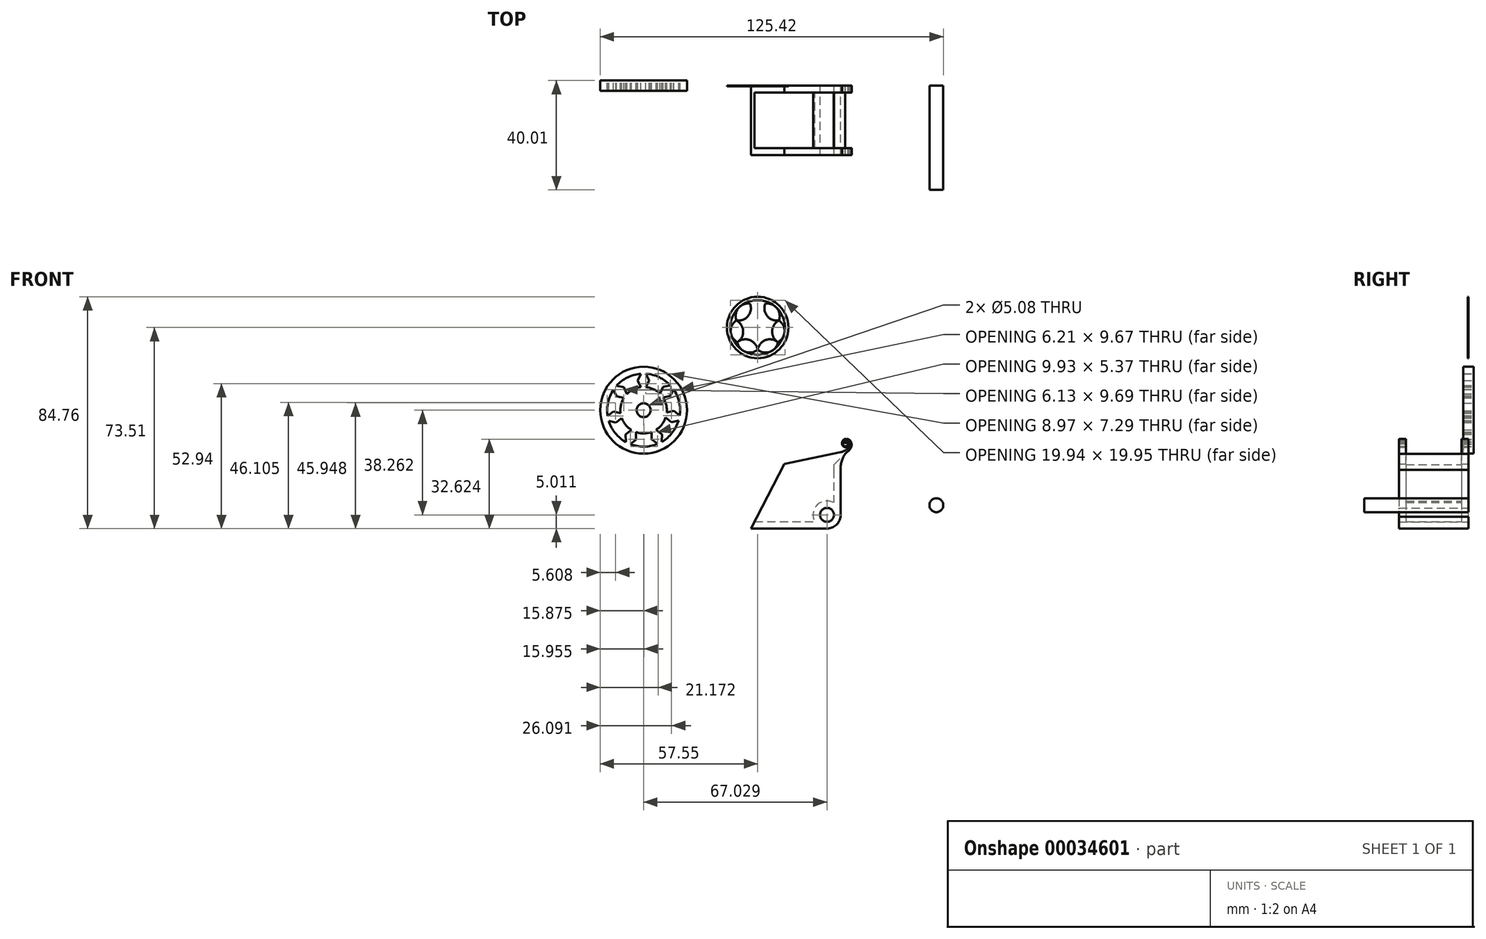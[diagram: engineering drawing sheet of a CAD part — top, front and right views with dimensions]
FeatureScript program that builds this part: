
annotation { "Feature Type Name" : "Feature", "Feature Type Description" : "" }
export const myFeature = defineFeature(function(context is Context, id is Id, definition is map)
    precondition{}
    {
        {
            var Q0;
            Q0=qCreatedBy(makeId("Front.planeOp"),FACE);
            var sketch = newSketch(context, id + "F0", { "sketchPlane" : qUnion([Q0])});
            skLineSegment(sketch, "E0", {"start": v(-14.54, -20.52) * mm, "end": v(13.23, -20.52) * mm});
            skLineSegment(sketch, "E1", {"start": v(18.2, 7.38) * mm, "end": v(-2.33, 3.11) * mm});
            skLineSegment(sketch, "E2", {"start": v(-2.33, 3.11) * mm, "end": v(-14.54, -20.52) * mm});
            skArc(sketch, "E3", {"start": v(13.23, -20.52) * mm, "mid": v(16.54, -19.27) * mm, "end": v(18.2, -16.16) * mm});
            skLineSegment(sketch, "E4.left", {"start": v(18.2, -0.57) * mm, "end": v(18.2, -0.57) * mm});
            skArc(sketch, "E5", {"start": v(18.2, 7.38) * mm, "mid": v(20.01, 8.1) * mm, "end": v(21.47, 9.4) * mm});
            skArc(sketch, "E6", {"start": v(21.47, 9.4) * mm, "mid": v(21.14, 11.42) * mm, "end": v(19.16, 10.9) * mm});
            skArc(sketch, "E7", {"start": v(19.16, 10.9) * mm, "mid": v(19.64, 9.63) * mm, "end": v(20.84, 10.26) * mm});
            skArc(sketch, "E8", {"start": v(20.84, 10.26) * mm, "mid": v(20.51, 10.8) * mm, "end": v(19.96, 10.48) * mm});
            skLineSegment(sketch, "E9", {"start": v(19.84, 6.78) * mm, "end": v(21.47, 8.34) * mm});
            skArc(sketch, "E10", {"start": v(21.47, 8.34) * mm, "mid": v(22.23, 10.05) * mm, "end": v(21.54, 11.8) * mm});
            skArc(sketch, "E11", {"start": v(21.54, 11.8) * mm, "mid": v(19.4, 11.99) * mm, "end": v(18.9, 9.88) * mm});
            skArc(sketch, "E12", {"start": v(18.9, 9.88) * mm, "mid": v(20.42, 9.3) * mm, "end": v(21.22, 10.7) * mm});
            skArc(sketch, "E13", {"start": v(21.22, 10.7) * mm, "mid": v(20.48, 11.2) * mm, "end": v(19.96, 10.48) * mm});
            skArc(sketch, "E14", {"start": v(19.84, 6.78) * mm, "mid": v(18.56, 4) * mm, "end": v(18.2, 0.95) * mm});
            skLineSegment(sketch, "E15.trimOffspring", {"start": v(18.2, 1.72) * mm, "end": v(18.2, -16.16) * mm});
            skPoint(sketch, "E16.end.orphan", {"position": v(18.2, 5.22) * mm});
            skCircle(sketch, "E17", {"center": v(13.23, -15.5) * mm, "radius": 2.54 * mm});
            skSolve(sketch);
        }
        {
            var Q0;
            Q0=makeQuery(id+"F0.imprint","IMPRINT",FACE,{"disambiguationData":[TD([[makeQuery(id+"F0.imprint","IMPRINT",EDGE,{"derivedFrom":sQuery(id+"F0.wireOp",EDGE,"E0")}),1.0]])]});
            extrude(context, id + "F1", {"entities" : qUnion([Q0]), "depth" : 25.4 * mm});
        }
        {
            var Q0;
            Q0=makeQuery(id+"F1.opExtrude","SWEPT_FACE",FACE,{"disambiguationData":[OSD([sQuery(id+"F0.wireOp",EDGE,"E2")])]});
            var Q1;
            Q1=makeQuery(id+"F1.opExtrude","SWEPT_FACE",FACE,{"disambiguationData":[OSD([sQuery(id+"F0.wireOp",EDGE,"E1")])]});
            var Q2;
            Q2=makeQuery(id+"F1.opExtrude","SWEPT_FACE",FACE,{"disambiguationData":[OSD([sQuery(id+"F0.wireOp",EDGE,"E8")])]});
            var Q3;
            Q3=makeQuery(id+"F1.opExtrude","SWEPT_FACE",FACE,{"disambiguationData":[OSD([sQuery(id+"F0.wireOp",EDGE,"E6")])]});
            var Q4;
            Q4=makeQuery(id+"F1.opExtrude","SWEPT_FACE",FACE,{"disambiguationData":[OSD([sQuery(id+"F0.wireOp",EDGE,"E5")])]});
            var Q5;
            Q5=makeQuery(id+"F1.opExtrude","SWEPT_FACE",FACE,{"disambiguationData":[OSD([sQuery(id+"F0.wireOp",EDGE,"E9")])]});
            var Q6;
            Q6=makeQuery(id+"F1.opExtrude","SWEPT_FACE",FACE,{"disambiguationData":[OSD([sQuery(id+"F0.wireOp",EDGE,"E12")])]});
            var Q7;
            Q7=makeQuery(id+"F1.opExtrude","SWEPT_FACE",FACE,{"disambiguationData":[OSD([sQuery(id+"F0.wireOp",EDGE,"E13")])]});
            var Q8;
            Q8=makeQuery(id+"F1.opExtrude","SWEPT_FACE",FACE,{"disambiguationData":[OSD([sQuery(id+"F0.wireOp",EDGE,"E7")])]});
            var Q9;
            Q9=makeQuery(id+"F1.opExtrude","SWEPT_FACE",FACE,{"disambiguationData":[OSD([sQuery(id+"F0.wireOp",EDGE,"E11")])]});
            var Q10;
            Q10=makeQuery(id+"F1.opExtrude","SWEPT_FACE",FACE,{"disambiguationData":[OSD([sQuery(id+"F0.wireOp",EDGE,"E10")])]});
            shell(context, id + "F2", {"entities" : qUnion([Q0, Q1, Q2, Q3, Q4, Q5, Q6, Q7, Q8, Q9, Q10]), "thickness" : 2.54 * mm});
        }
        {
            var Q0;
            Q0=qCreatedBy(makeId("Front.planeOp"),FACE);
            var sketch = newSketch(context, id + "F3", { "sketchPlane" : qUnion([Q0])});
            skCircle(sketch, "E18", {"center": v(-53.8, 22.75) * mm, "radius": 13.33 * mm});
            skCircle(sketch, "E19.0", {"center": v(-53.8, 22.75) * mm, "radius": 15.88 * mm});
            skCircle(sketch, "E20", {"center": v(-53.8, 22.75) * mm, "radius": 8.49 * mm});
            skPoint(sketch, "E21.end.orphan", {"position": v(-46.16, 26.45) * mm});
            skPoint(sketch, "E22.end.orphan", {"position": v(-53.8, 31.24) * mm});
            skPoint(sketch, "E23.start.orphan", {"position": v(-61.43, 26.45) * mm});
            skPoint(sketch, "E24.start.orphan", {"position": v(-53.8, 14.27) * mm});
            skPoint(sketch, "E25.start.orphan", {"position": v(-46.16, 19.06) * mm});
            skCircle(sketch, "E26", {"center": v(-53.8, 22.75) * mm, "radius": 2.54 * mm});
            skLineSegment(sketch, "E27", {"start": v(-54.78, 36.05) * mm, "end": v(-55.99, 33.62) * mm});
            skLineSegment(sketch, "E28", {"start": v(-55.99, 33.62) * mm, "end": v(-54.78, 31.18) * mm});
            skLineSegment(sketch, "E29", {"start": v(-52.99, 31.2) * mm, "end": v(-51.77, 33.62) * mm});
            skLineSegment(sketch, "E30", {"start": v(-51.77, 33.62) * mm, "end": v(-52.99, 36.06) * mm});
            skLineSegment(sketch, "E31.1.0", {"start": v(-61.03, 31.11) * mm, "end": v(-63.7, 31.69) * mm});
            skLineSegment(sketch, "E31.1.1", {"start": v(-59.9, 28.65) * mm, "end": v(-61.03, 31.11) * mm});
            skLineSegment(sketch, "E31.1.2", {"start": v(-63.66, 27.82) * mm, "end": v(-61, 27.24) * mm});
            skLineSegment(sketch, "E31.1.3", {"start": v(-64.8, 30.28) * mm, "end": v(-63.66, 27.82) * mm});
            skLineSegment(sketch, "E31.2.0", {"start": v(-64.84, 22.3) * mm, "end": v(-66.95, 20.58) * mm});
            skLineSegment(sketch, "E31.2.1", {"start": v(-62.21, 21.66) * mm, "end": v(-64.84, 22.3) * mm});
            skLineSegment(sketch, "E31.2.2", {"start": v(-63.9, 18.2) * mm, "end": v(-61.8, 19.92) * mm});
            skLineSegment(sketch, "E31.2.3", {"start": v(-66.54, 18.83) * mm, "end": v(-63.9, 18.2) * mm});
            skLineSegment(sketch, "E32.1.3.0", {"start": v(-60.34, 13.84) * mm, "end": v(-60.3, 11.11) * mm});
            skLineSegment(sketch, "E32.3.3.0", {"start": v(-58.2, 15.5) * mm, "end": v(-60.34, 13.84) * mm});
            skLineSegment(sketch, "E32.6.3.0", {"start": v(-56.54, 12) * mm, "end": v(-56.57, 14.73) * mm});
            skLineSegment(sketch, "E32.9.3.0", {"start": v(-58.68, 10.34) * mm, "end": v(-56.54, 12) * mm});
            skLineSegment(sketch, "E32.1.4.0", {"start": v(-50.9, 12.08) * mm, "end": v(-48.75, 10.4) * mm});
            skLineSegment(sketch, "E32.3.4.0", {"start": v(-50.86, 14.8) * mm, "end": v(-50.9, 12.08) * mm});
            skLineSegment(sketch, "E32.6.4.0", {"start": v(-47.1, 13.9) * mm, "end": v(-49.25, 15.59) * mm});
            skLineSegment(sketch, "E32.9.4.0", {"start": v(-47.14, 11.2) * mm, "end": v(-47.1, 13.9) * mm});
            skLineSegment(sketch, "E33.1.5.0", {"start": v(-43.65, 18.36) * mm, "end": v(-41, 19) * mm});
            skLineSegment(sketch, "E33.3.5.0", {"start": v(-45.74, 20.08) * mm, "end": v(-43.65, 18.36) * mm});
            skLineSegment(sketch, "E33.6.5.0", {"start": v(-42.7, 22.47) * mm, "end": v(-45.36, 21.84) * mm});
            skLineSegment(sketch, "E33.9.5.0", {"start": v(-40.61, 20.75) * mm, "end": v(-42.7, 22.47) * mm});
            skLineSegment(sketch, "E33.1.6.0", {"start": v(-44.03, 27.95) * mm, "end": v(-42.88, 30.42) * mm});
            skLineSegment(sketch, "E33.3.6.0", {"start": v(-46.69, 27.39) * mm, "end": v(-44.03, 27.95) * mm});
            skLineSegment(sketch, "E33.6.6.0", {"start": v(-46.66, 31.24) * mm, "end": v(-47.82, 28.78) * mm});
            skLineSegment(sketch, "E33.9.6.0", {"start": v(-44.01, 31.81) * mm, "end": v(-46.66, 31.24) * mm});
            skSolve(sketch);
        }
        {
            var Q0;
            Q0=makeQuery(id+"F3.imprint","IMPRINT",FACE,{"disambiguationData":[TD([[makeQuery(id+"F3.imprint","IMPRINT",EDGE,{"derivedFrom":sQuery(id+"F3.wireOp",EDGE,"E19.0")}),1.0]])]});
            var Q1;
            {var subQ0=sQuery(id+"F3.wireOp",EDGE,"E20");var subQ8=makeQuery(id+"F3.imprint","IMPRINT",VERTEX,{"disambiguationData":[OD(0.0)],"derivedFrom":subQ0});Q1=makeQuery(id+"F3.imprint","IMPRINT",FACE,{"disambiguationData":[TD([[makeQuery(id+"F3.imprint","IMPRINT",EDGE,{"disambiguationData":[TD([[subQ8,1.0]])],"derivedFrom":subQ0}),1.0]])]});}
            var Q2;
            {var subQ0=sQuery(id+"F3.wireOp",EDGE,"E20");var subQ2=makeQuery(id+"F3.imprint","INTERSECT",VERTEX,{"derivedFrom":[subQ0,sQuery(id+"F3.wireOp",EDGE,"E21")]});Q2=makeQuery(id+"F3.imprint","IMPRINT",FACE,{"disambiguationData":[TD([[makeQuery(id+"F3.imprint","IMPRINT",EDGE,{"disambiguationData":[TD([[subQ2,-1.0]])],"derivedFrom":subQ0}),1.0]])]});}
            var Q3;
            Q3=makeQuery(id+"F3.imprint","IMPRINT",FACE,{"disambiguationData":[TD([[makeQuery(id+"F3.imprint","IMPRINT",EDGE,{"derivedFrom":sQuery(id+"F3.wireOp",EDGE,"E20")}),1.0]])]});
            var Q4;
            {var subQ3=sQuery(id+"F3.wireOp",EDGE,"E27");Q4=makeQuery(id+"F3.imprint","IMPRINT",FACE,{"disambiguationData":[TD([[makeQuery(id+"F3.imprint","IMPRINT",EDGE,{"derivedFrom":subQ3}),1.0]])]});}
            var Q5;
            {var subQ3=sQuery(id+"F3.wireOp",EDGE,"E33.1.6.0");Q5=makeQuery(id+"F3.imprint","IMPRINT",FACE,{"disambiguationData":[TD([[makeQuery(id+"F3.imprint","IMPRINT",EDGE,{"derivedFrom":subQ3}),1.0]])]});}
            var Q6;
            {var subQ2=sQuery(id+"F3.wireOp",EDGE,"E33.1.5.0");Q6=makeQuery(id+"F3.imprint","IMPRINT",FACE,{"disambiguationData":[TD([[makeQuery(id+"F3.imprint","IMPRINT",EDGE,{"derivedFrom":subQ2}),1.0]])]});}
            var Q7;
            {var subQ4=sQuery(id+"F3.wireOp",EDGE,"E32.1.4.0");Q7=makeQuery(id+"F3.imprint","IMPRINT",FACE,{"disambiguationData":[TD([[makeQuery(id+"F3.imprint","IMPRINT",EDGE,{"derivedFrom":subQ4}),1.0]])]});}
            var Q8;
            {var subQ3=sQuery(id+"F3.wireOp",EDGE,"E32.1.3.0");Q8=makeQuery(id+"F3.imprint","IMPRINT",FACE,{"disambiguationData":[TD([[makeQuery(id+"F3.imprint","IMPRINT",EDGE,{"derivedFrom":subQ3}),1.0]])]});}
            var Q9;
            {var subQ3=sQuery(id+"F3.wireOp",EDGE,"E31.2.0");Q9=makeQuery(id+"F3.imprint","IMPRINT",FACE,{"disambiguationData":[TD([[makeQuery(id+"F3.imprint","IMPRINT",EDGE,{"derivedFrom":subQ3}),1.0]])]});}
            var Q10;
            {var subQ3=sQuery(id+"F3.wireOp",EDGE,"E31.1.0");Q10=makeQuery(id+"F3.imprint","IMPRINT",FACE,{"disambiguationData":[TD([[makeQuery(id+"F3.imprint","IMPRINT",EDGE,{"derivedFrom":subQ3}),1.0]])]});}
            extrude(context, id + "F4", {"entities" : qUnion([Q0, Q1, Q2, Q3, Q4, Q5, Q6, Q7, Q8, Q9, Q10]), "endBound" : BoundingType.SYMMETRIC, "depth" : 3.8 * mm});
        }
        {
            var Q0;
            Q0=qCreatedBy(makeId("Front.planeOp"),FACE);
            var sketch = newSketch(context, id + "F5", { "sketchPlane" : qUnion([Q0])});
            skCircle(sketch, "E34", {"center": v(53.2, -11.99) * mm, "radius": 2.54 * mm});
            skSolve(sketch);
        }
        {
            var Q0;
            Q0 = qSketchRegion(id + "F5", true);
            extrude(context, id + "F6", {"entities" : qUnion([Q0]), "depth" : 38.1 * mm});
        }
        {
            var Q0;
            Q0=qCreatedBy(makeId("Front.planeOp"),FACE);
            var sketch = newSketch(context, id + "F7", { "sketchPlane" : qUnion([Q0])});
            skArc(sketch, "E35", {"start": v(-12.12, 44.83) * mm, "mid": v(-15.02, 48.37) * mm, "end": v(-19.53, 47.63) * mm});
            skPoint(sketch, "E35.startSnap0", {"position": v(-12.12, 44.83) * mm});
            skArc(sketch, "E36", {"start": v(-19.53, 47.63) * mm, "mid": v(-16.63, 44.1) * mm, "end": v(-12.12, 44.83) * mm});
            skArc(sketch, "E37", {"start": v(-19.53, 47.63) * mm, "mid": v(-17.42, 51.69) * mm, "end": v(-19.87, 55.54) * mm});
            skArc(sketch, "E38", {"start": v(-19.87, 55.54) * mm, "mid": v(-21.98, 51.49) * mm, "end": v(-19.53, 47.63) * mm});
            skArc(sketch, "E39", {"start": v(-14.9, 61.7) * mm, "mid": v(-19.16, 60.06) * mm, "end": v(-19.87, 55.54) * mm});
            skArc(sketch, "E40", {"start": v(-19.87, 55.54) * mm, "mid": v(-15.6, 57.18) * mm, "end": v(-14.9, 61.7) * mm});
            skArc(sketch, "E41", {"start": v(-4.37, 55.54) * mm, "mid": v(-5.08, 60.06) * mm, "end": v(-9.35, 61.7) * mm});
            skArc(sketch, "E42", {"start": v(-9.35, 61.7) * mm, "mid": v(-8.64, 57.18) * mm, "end": v(-4.37, 55.54) * mm});
            skArc(sketch, "E43", {"start": v(-4.71, 47.63) * mm, "mid": v(-2.26, 51.49) * mm, "end": v(-4.37, 55.54) * mm});
            skArc(sketch, "E44", {"start": v(-4.37, 55.54) * mm, "mid": v(-6.82, 51.69) * mm, "end": v(-4.71, 47.63) * mm});
            skArc(sketch, "E45", {"start": v(-12.12, 44.83) * mm, "mid": v(-7.6, 44.1) * mm, "end": v(-4.71, 47.63) * mm});
            skArc(sketch, "E46", {"start": v(-4.71, 47.63) * mm, "mid": v(-9.23, 48.37) * mm, "end": v(-12.12, 44.83) * mm});
            skLineSegment(sketch, "E47", {"start": v(-12.12, 44.83) * mm, "end": v(-12.12, 44.83) * mm});
            skCircle(sketch, "E48", {"center": v(-12.12, 52.99) * mm, "radius": 9.98 * mm});
            skCircle(sketch, "E49", {"center": v(-12.12, 52.99) * mm, "radius": 11.25 * mm});
            skSolve(sketch);
        }
        {
            var Q0;
            Q0 = qSketchRegion(id + "F7", true);
            var Q1;
            {var subQ4=sQuery(id+"F7.wireOp",EDGE,"E40");Q1=makeQuery(id+"F7.imprint","IMPRINT",FACE,{"disambiguationData":[TD([[makeQuery(id+"F7.imprint","IMPRINT",EDGE,{"derivedFrom":subQ4}),1.0]])]});}
            var Q2;
            {var subQ0=sQuery(id+"F7.wireOp",EDGE,"E48");var subQ1=sQuery(id+"F7.wireOp",EDGE,"E38");var subQ3=makeQuery(id+"F7.imprint","INTERSECT",VERTEX,{"disambiguationData":[OD(0.0)],"derivedFrom":[subQ1,subQ0]});Q2=makeQuery(id+"F7.imprint","IMPRINT",FACE,{"disambiguationData":[TD([[makeQuery(id+"F7.imprint","IMPRINT",EDGE,{"disambiguationData":[TD([[subQ3,-1.0]])],"derivedFrom":subQ0}),1.0]])]});}
            var Q3;
            {var subQ0=sQuery(id+"F7.wireOp",EDGE,"E48");var subQ1=sQuery(id+"F7.wireOp",EDGE,"E36");var subQ3=makeQuery(id+"F7.imprint","INTERSECT",VERTEX,{"disambiguationData":[OD(0.0)],"derivedFrom":[subQ1,subQ0]});Q3=makeQuery(id+"F7.imprint","IMPRINT",FACE,{"disambiguationData":[TD([[makeQuery(id+"F7.imprint","IMPRINT",EDGE,{"disambiguationData":[TD([[subQ3,-1.0]])],"derivedFrom":subQ0}),1.0]])]});}
            var Q4;
            {var subQ0=sQuery(id+"F7.wireOp",EDGE,"E48");var subQ1=sQuery(id+"F7.wireOp",EDGE,"E45");var subQ3=makeQuery(id+"F7.imprint","INTERSECT",VERTEX,{"disambiguationData":[OD(0.0)],"derivedFrom":[subQ1,subQ0]});Q4=makeQuery(id+"F7.imprint","IMPRINT",FACE,{"disambiguationData":[TD([[makeQuery(id+"F7.imprint","IMPRINT",EDGE,{"disambiguationData":[TD([[subQ3,-1.0]])],"derivedFrom":subQ0}),1.0]])]});}
            var Q5;
            {var subQ0=sQuery(id+"F7.wireOp",EDGE,"E48");var subQ1=sQuery(id+"F7.wireOp",EDGE,"E43");var subQ3=makeQuery(id+"F7.imprint","INTERSECT",VERTEX,{"disambiguationData":[OD(0.0)],"derivedFrom":[subQ1,subQ0]});Q5=makeQuery(id+"F7.imprint","IMPRINT",FACE,{"disambiguationData":[TD([[makeQuery(id+"F7.imprint","IMPRINT",EDGE,{"disambiguationData":[TD([[subQ3,-1.0]])],"derivedFrom":subQ0}),1.0]])]});}
            var Q6;
            {var subQ4=sQuery(id+"F7.wireOp",EDGE,"E42");Q6=makeQuery(id+"F7.imprint","IMPRINT",FACE,{"disambiguationData":[TD([[makeQuery(id+"F7.imprint","IMPRINT",EDGE,{"derivedFrom":subQ4}),1.0]])]});}
            extrude(context, id + "F8", {"entities" : qUnion([Q0, Q1, Q2, Q3, Q4, Q5, Q6]), "depth" : 0.25 * mm});
        }
    });
